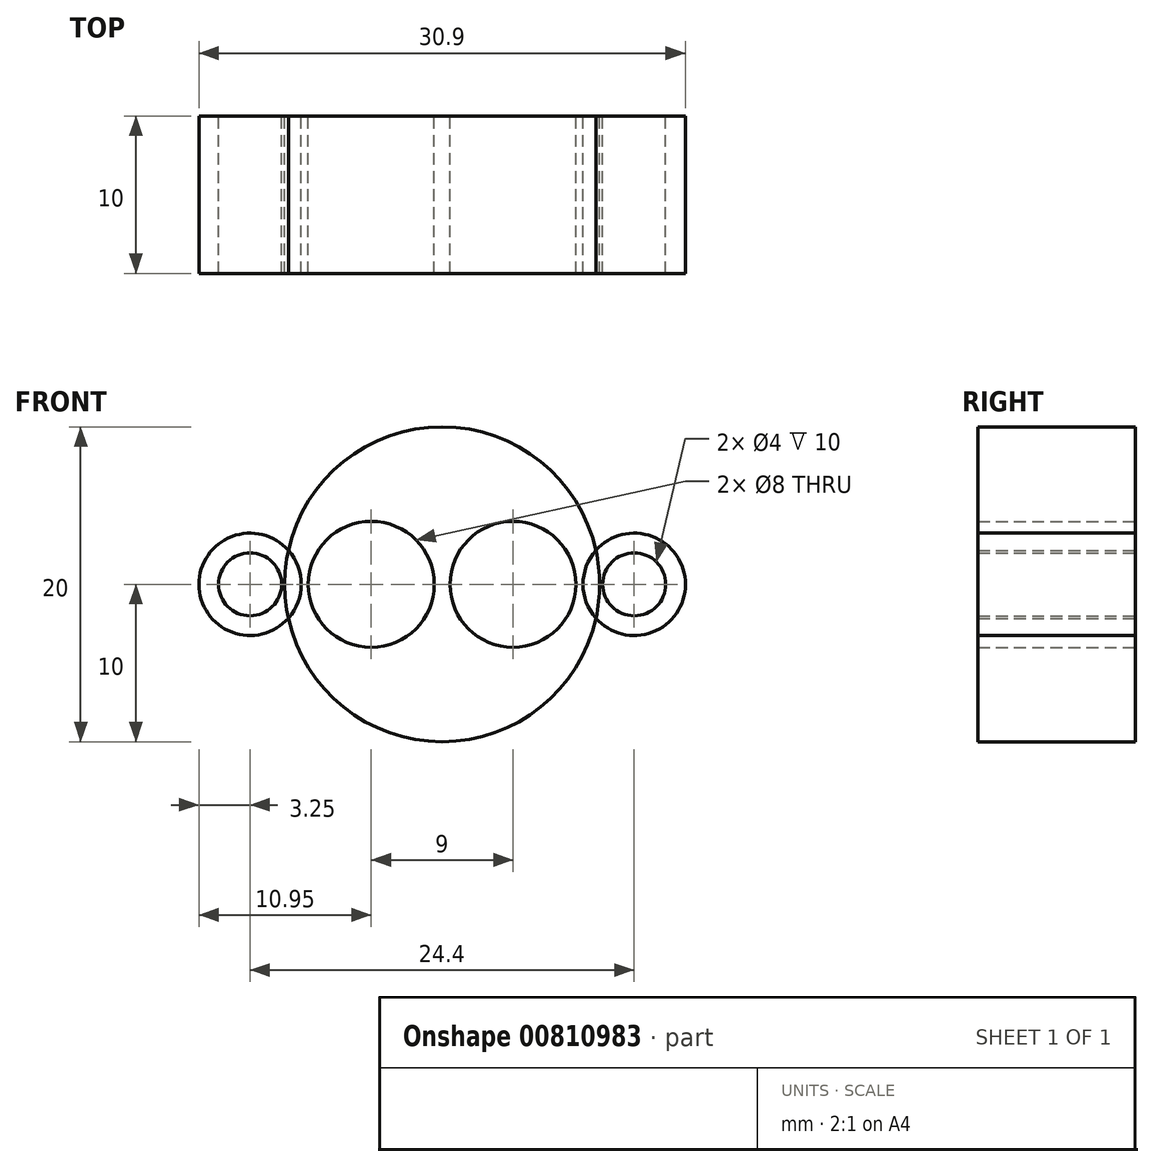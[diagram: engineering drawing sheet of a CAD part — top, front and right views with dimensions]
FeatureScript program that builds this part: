
annotation { "Feature Type Name" : "Feature", "Feature Type Description" : "" }
export const myFeature = defineFeature(function(context is Context, id is Id, definition is map)
    precondition{}
    {
        {
            var Q0;
            Q0=qCreatedBy(makeId("Front.planeOp"),FACE);
            var sketch = newSketch(context, id + "F0", { "sketchPlane" : qUnion([Q0])});
            skCircle(sketch, "E0", {"center": v(0, 0) * mm, "radius": 10 * mm});
            skCircle(sketch, "E1", {"center": v(-4.5, 0) * mm, "radius": 4 * mm});
            skCircle(sketch, "E2", {"center": v(4.5, 0) * mm, "radius": 4 * mm});
            skCircle(sketch, "E3", {"center": v(-12.2, 0) * mm, "radius": 3.25 * mm});
            skCircle(sketch, "E4", {"center": v(-12.2, 0) * mm, "radius": 2 * mm});
            skCircle(sketch, "E5", {"center": v(12.2, 0) * mm, "radius": 3.25 * mm});
            skCircle(sketch, "E6", {"center": v(12.2, 0) * mm, "radius": 2 * mm});
            skPoint(sketch, "E7.middle", {"position": v(0, 10) * mm});
            skPoint(sketch, "E8.middle", {"position": v(0, -10) * mm});
            skSolve(sketch);
        }
        {
            var Q0;
            Q0=makeQuery(id+"F0.imprint","IMPRINT",FACE,{"disambiguationData":[TD([[makeQuery(id+"F0.imprint","IMPRINT",EDGE,{"derivedFrom":sQuery(id+"F0.wireOp",EDGE,"E0")}),1.0]])]});
            extrude(context, id + "F1", {"entities" : qUnion([Q0]), "depth" : 10 * mm, "offsetDistance" : 25 * mm});
        }
        {
            var Q0;
            {var subQ0=sQuery(id+"F0.wireOp",EDGE,"E3");var subQ1=sQuery(id+"F0.wireOp",EDGE,"E0");var subQ2=makeQuery(id+"F0.imprint","INTERSECT",VERTEX,{"disambiguationData":[OD(0.0)],"derivedFrom":[subQ1,subQ0]});Q0=makeQuery(id+"F0.imprint","IMPRINT",FACE,{"disambiguationData":[TD([[makeQuery(id+"F0.imprint","IMPRINT",EDGE,{"disambiguationData":[TD([[subQ2,-1.0]])],"derivedFrom":subQ1}),-1.0]])]});}
            var Q1;
            {var subQ0=sQuery(id+"F0.wireOp",EDGE,"E5");var subQ1=sQuery(id+"F0.wireOp",EDGE,"E0");var subQ2=makeQuery(id+"F0.imprint","INTERSECT",VERTEX,{"disambiguationData":[OD(0.0)],"derivedFrom":[subQ1,subQ0]});Q1=makeQuery(id+"F0.imprint","IMPRINT",FACE,{"disambiguationData":[TD([[makeQuery(id+"F0.imprint","IMPRINT",EDGE,{"disambiguationData":[TD([[subQ2,1.0]])],"derivedFrom":subQ1}),-1.0]])]});}
            extrude(context, id + "F2", {"entities" : qUnion([Q0, Q1]), "depth" : 10 * mm, "offsetDistance" : 25 * mm});
        }
        {
            var Q0;
            {var subQ0=sQuery(id+"F0.wireOp",EDGE,"E5");var subQ1=sQuery(id+"F0.wireOp",EDGE,"E0");var subQ2=makeQuery(id+"F0.imprint","INTERSECT",VERTEX,{"disambiguationData":[OD(0.0)],"derivedFrom":[subQ1,subQ0]});Q0=makeQuery(id+"F0.imprint","IMPRINT",FACE,{"disambiguationData":[TD([[makeQuery(id+"F0.imprint","IMPRINT",EDGE,{"disambiguationData":[TD([[subQ2,1.0]])],"derivedFrom":subQ1}),1.0]])]});}
            var Q1;
            {var subQ0=sQuery(id+"F0.wireOp",EDGE,"E3");var subQ1=sQuery(id+"F0.wireOp",EDGE,"E0");var subQ2=makeQuery(id+"F0.imprint","INTERSECT",VERTEX,{"disambiguationData":[OD(0.0)],"derivedFrom":[subQ1,subQ0]});Q1=makeQuery(id+"F0.imprint","IMPRINT",FACE,{"disambiguationData":[TD([[makeQuery(id+"F0.imprint","IMPRINT",EDGE,{"disambiguationData":[TD([[subQ2,-1.0]])],"derivedFrom":subQ1}),1.0]])]});}
            extrude(context, id + "F3", {"entities" : qUnion([Q0, Q1]), "depth" : 10 * mm, "offsetDistance" : 25 * mm});
        }
    });
